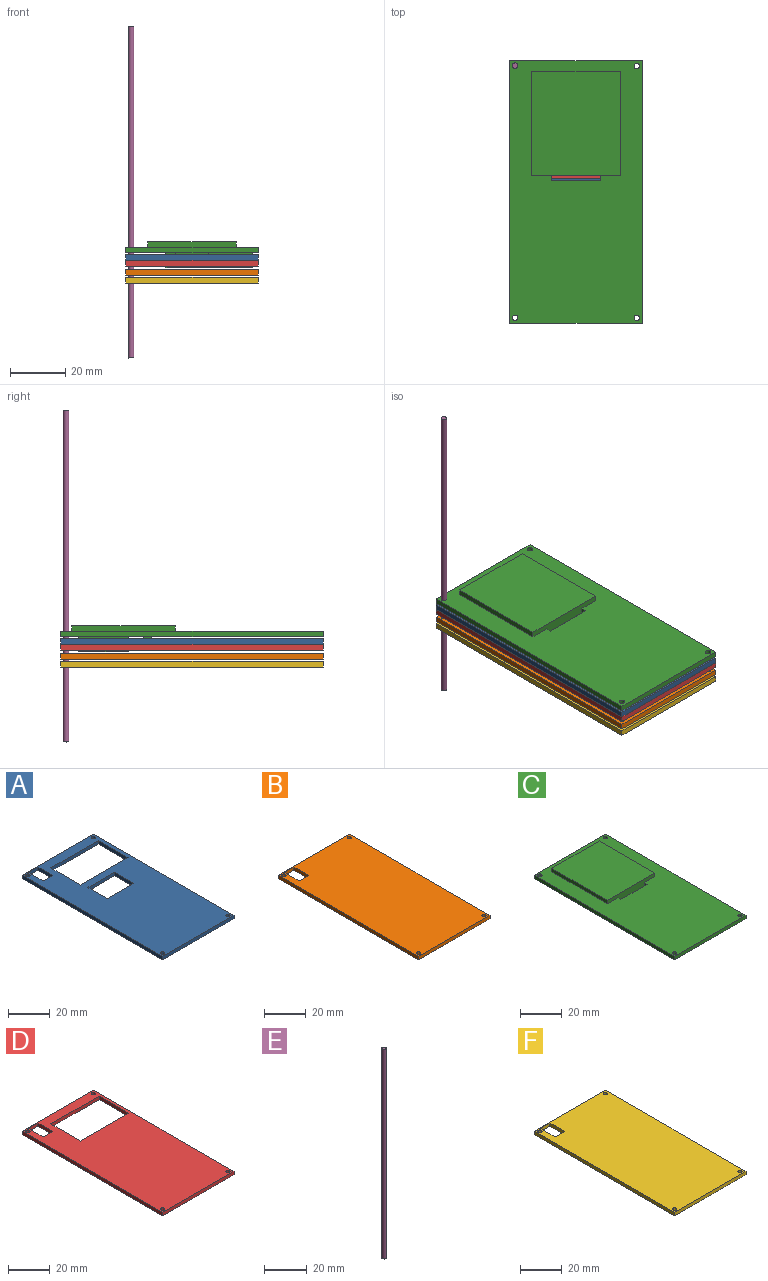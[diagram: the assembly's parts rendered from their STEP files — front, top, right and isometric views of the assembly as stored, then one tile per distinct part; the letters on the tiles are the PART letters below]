
ASSEMBLY  parts=6 mates=6
PART A: 22 faces, bbox 48x95x2 mm
  f0: plane 95x48mm, normal (0,0,1), area 3609.4mm2, adj f2,f3,f4,f5,f6,f7,f8,f9
  f1: plane 95x48mm, normal (0,0,-1), area 3609.4mm2, adj f2,f3,f4,f5,f6,f7,f8,f9
  f2: plane 48x2mm, normal (0,-1,0), area 96mm2, adj f0,f1,f3,f8
  f3: plane 95x2mm, normal (1,0,0), area 190mm2, adj f0,f1,f2,f4
  f4: plane 48x2mm, normal (0,1,0), area 96mm2, adj f0,f1,f3,f8
  f5: cylinder r=1mm len=2mm, axis (0,0,-1), area 12.6mm2, adj f0,f1
  f6: cylinder r=1mm len=2mm, axis (0,0,-1), area 12.6mm2, adj f0,f1
  f7: cylinder r=1mm len=2mm, axis (0,0,-1), area 12.6mm2, adj f0,f1
  f8: plane 95x2mm, normal (-1,0,0), area 190mm2, adj f0,f1,f2,f4
  f9: cylinder r=1mm len=2mm, axis (0,0,-1), area 12.6mm2, adj f0,f1
  f10: plane 18x2mm, normal (0,1,0), area 36mm2, adj f0,f1,f11,f13
  f11: plane 13x2mm, normal (1,0,0), area 26mm2, adj f0,f1,f10,f12
  f12: plane 18x2mm, normal (0,-1,0), area 36mm2, adj f0,f1,f11,f13
  f13: plane 13x2mm, normal (-1,0,0), area 26mm2, adj f0,f1,f10,f12
  f14: plane 20x2mm, normal (1,0,0), area 40mm2, adj f0,f1,f15,f17
  f15: plane 32x2mm, normal (0,1,0), area 64mm2, adj f0,f1,f14,f16
  f16: plane 20x2mm, normal (-1,0,0), area 40mm2, adj f0,f1,f15,f17
  f17: plane 32x2mm, normal (0,-1,0), area 64mm2, adj f0,f1,f14,f16
  f18: plane 6.4x2mm, normal (0,1,0), area 12.8mm2, adj f0,f1,f19,f21
  f19: plane 10x2mm, normal (-1,0,0), area 20mm2, adj f0,f1,f18,f20
  f20: plane 6.4x2mm, normal (0,-1,0), area 12.8mm2, adj f0,f1,f19,f21
  f21: plane 10x2mm, normal (1,0,0), area 20mm2, adj f0,f1,f18,f20
PART B: 14 faces, bbox 48x95x2 mm
  f0: plane 95x2mm, normal (-1,0,0), area 190mm2, adj f1,f7,f8,f9
  f1: plane 48x2mm, normal (0,-1,0), area 96mm2, adj f0,f2,f8,f9
  f2: plane 95x2mm, normal (1,0,0), area 190mm2, adj f1,f7,f8,f9
  f3: cylinder r=1mm len=2mm, axis (0,0,-1), area 12.6mm2, adj f8,f9
  f4: cylinder r=1mm len=2mm, axis (0,0,-1), area 12.6mm2, adj f8,f9
  f5: cylinder r=1mm len=2mm, axis (0,0,-1), area 12.6mm2, adj f8,f9
  f6: cylinder r=1mm len=2mm, axis (0,0,-1), area 12.6mm2, adj f8,f9
  f7: plane 48x2mm, normal (0,1,0), area 96mm2, adj f0,f2,f8,f9
  f8: plane 95x48mm, normal (0,0,1), area 4483.4mm2, adj f0,f1,f2,f3,f4,f5,f6,f7
  f9: plane 95x48mm, normal (0,0,-1), area 4483.4mm2, adj f0,f1,f2,f3,f4,f5,f6,f7
  f10: plane 6.4x2mm, normal (0,1,0), area 12.8mm2, adj f8,f9,f11,f13
  f11: plane 10x2mm, normal (-1,0,0), area 20mm2, adj f8,f9,f10,f12
  f12: plane 6.4x2mm, normal (0,-1,0), area 12.8mm2, adj f8,f9,f11,f13
  f13: plane 10x2mm, normal (1,0,0), area 20mm2, adj f8,f9,f10,f12
PART C: 28 faces, bbox 48x95x9.3 mm
  f0: plane 95x48mm, normal (0,0,-1), area 3910.2mm2, adj f2,f3,f4,f5,f6,f7,f8,f9
  f1: plane 95x48mm, normal (0,0,1), area 3311.4mm2, adj f2,f3,f4,f5,f6,f7,f8,f9
  f2: plane 48x2mm, normal (0,-1,0), area 96mm2, adj f0,f1,f3,f8
  f3: plane 95x2mm, normal (1,0,0), area 190mm2, adj f0,f1,f2,f4
  f4: plane 48x2mm, normal (0,1,0), area 96mm2, adj f0,f1,f3,f8
  f5: cylinder r=1mm len=2mm, axis (0,0,-1), area 12.6mm2, adj f0,f1
  f6: cylinder r=1mm len=2mm, axis (0,0,-1), area 12.6mm2, adj f0,f1
  f7: cylinder r=1mm len=2mm, axis (0,0,-1), area 12.6mm2, adj f0,f1
  f8: plane 95x2mm, normal (-1,0,0), area 190mm2, adj f0,f1,f2,f4
  f9: cylinder r=1mm len=2mm, axis (0,0,-1), area 12.6mm2, adj f0,f1
  f10: plane 18x2mm, normal (0,1,0), area 36mm2, adj f0,f1,f11,f13
  f11: plane 2x2mm, normal (1,0,0), area 4mm2, adj f0,f1,f10,f12
  f12: plane 32x4mm, normal (0,-1,0), area 100mm2, adj f0,f1,f11,f13,f14,f16,f17
  f13: plane 2x2mm, normal (-1,0,0), area 4mm2, adj f0,f1,f10,f12
  f14: plane 37.5x2mm, normal (1,0,0), area 75mm2, adj f1,f12,f15,f17
  f15: plane 32x2mm, normal (0,1,0), area 64mm2, adj f1,f14,f16,f17
  f16: plane 37.5x2mm, normal (-1,0,0), area 75mm2, adj f1,f12,f15,f17
  f17: plane 37.5x32mm, normal (0,0,1), area 1200mm2, adj f12,f14,f15,f16
  f18: plane 3x2mm, normal (-1,0,0), area 6mm2, adj f0,f19,f21,f22
  f19: plane 12x2mm, normal (0,-1,0), area 24mm2, adj f0,f18,f20,f22
  f20: plane 3x2mm, normal (1,0,0), area 6mm2, adj f0,f19,f21,f22
  f21: plane 12x2mm, normal (0,1,0), area 24mm2, adj f0,f18,f20,f22
  f22: plane 12x3mm, normal (0,0,-1), area 36mm2, adj f18,f19,f20,f21
  f23: plane 18x5.3mm, normal (-1,0,0), area 95.4mm2, adj f0,f24,f26,f27
  f24: plane 31.4x5.3mm, normal (0,-1,0), area 166.4mm2, adj f0,f23,f25,f27
  f25: plane 18x5.3mm, normal (1,0,0), area 95.4mm2, adj f0,f24,f26,f27
  f26: plane 31.4x5.3mm, normal (0,1,0), area 166.4mm2, adj f0,f23,f25,f27
  f27: plane 31.4x18mm, normal (0,0,-1), area 565.2mm2, adj f23,f24,f25,f26
PART D: 18 faces, bbox 48x95x2 mm
  f0: plane 48x2mm, normal (0,-1,0), area 96mm2, adj f1,f6,f8,f9
  f1: plane 95x2mm, normal (1,0,0), area 190mm2, adj f0,f2,f8,f9
  f2: plane 48x2mm, normal (0,1,0), area 96mm2, adj f1,f6,f8,f9
  f3: cylinder r=1mm len=2mm, axis (0,0,-1), area 12.6mm2, adj f8,f9
  f4: cylinder r=1mm len=2mm, axis (0,0,-1), area 12.6mm2, adj f8,f9
  f5: cylinder r=1mm len=2mm, axis (0,0,-1), area 12.6mm2, adj f8,f9
  f6: plane 95x2mm, normal (-1,0,0), area 190mm2, adj f0,f2,f8,f9
  f7: cylinder r=1mm len=2mm, axis (0,0,-1), area 12.6mm2, adj f8,f9
  f8: plane 95x48mm, normal (0,0,1), area 3833.4mm2, adj f0,f1,f2,f3,f4,f5,f6,f7
  f9: plane 95x48mm, normal (0,0,-1), area 3833.4mm2, adj f0,f1,f2,f3,f4,f5,f6,f7
  f10: plane 6.4x2mm, normal (0,1,0), area 12.8mm2, adj f8,f9,f11,f13
  f11: plane 10x2mm, normal (-1,0,0), area 20mm2, adj f8,f9,f10,f12
  f12: plane 6.4x2mm, normal (0,-1,0), area 12.8mm2, adj f8,f9,f11,f13
  f13: plane 10x2mm, normal (1,0,0), area 20mm2, adj f8,f9,f10,f12
  f14: plane 20x2mm, normal (1,0,0), area 40mm2, adj f8,f9,f15,f17
  f15: plane 32.5x2mm, normal (0,1,0), area 65mm2, adj f8,f9,f14,f16
  f16: plane 20x2mm, normal (-1,0,0), area 40mm2, adj f8,f9,f15,f17
  f17: plane 32.5x2mm, normal (0,-1,0), area 65mm2, adj f8,f9,f14,f16
PART E: 3 faces, bbox 2x2x120 mm
  f0: cylinder r=1mm len=120mm, axis (0,0,-1), area 754mm2, adj f1,f2
  f1: plane 2x2mm, normal (0,0,1), area 3.1mm2, adj f0
  f2: plane 2x2mm, normal (0,0,-1), area 3.1mm2, adj f0
PART F: 14 faces, bbox 48x95x2 mm
  f0: plane 95x2mm, normal (-1,0,0), area 190mm2, adj f1,f7,f8,f9
  f1: plane 48x2mm, normal (0,-1,0), area 96mm2, adj f0,f2,f8,f9
  f2: plane 95x2mm, normal (1,0,0), area 190mm2, adj f1,f7,f8,f9
  f3: cylinder r=1mm len=2mm, axis (0,0,-1), area 12.6mm2, adj f8,f9
  f4: cylinder r=1mm len=2mm, axis (0,0,-1), area 12.6mm2, adj f8,f9
  f5: cylinder r=1mm len=2mm, axis (0,0,-1), area 12.6mm2, adj f8,f9
  f6: cylinder r=1mm len=2mm, axis (0,0,-1), area 12.6mm2, adj f8,f9
  f7: plane 48x2mm, normal (0,1,0), area 96mm2, adj f0,f2,f8,f9
  f8: plane 95x48mm, normal (0,0,1), area 4483.4mm2, adj f0,f1,f2,f3,f4,f5,f6,f7
  f9: plane 95x48mm, normal (0,0,-1), area 4483.4mm2, adj f0,f1,f2,f3,f4,f5,f6,f7
  f10: plane 6.4x2mm, normal (0,1,0), area 12.8mm2, adj f8,f9,f11,f13
  f11: plane 10x2mm, normal (-1,0,0), area 20mm2, adj f8,f9,f10,f12
  f12: plane 6.4x2mm, normal (0,-1,0), area 12.8mm2, adj f8,f9,f11,f13
  f13: plane 10x2mm, normal (1,0,0), area 20mm2, adj f8,f9,f10,f12
PLACE A t=(-49.24,-191.65,86.66)mm
PLACE B t=(-149.24,-191.65,81.3)mm
PLACE C t=(0.76,-191.65,89.31)mm
PLACE D t=(-99.24,-191.65,84.56)mm
PLACE E t=(-496.24,-96.65,51.32)mm
PLACE F t=(-199.24,-191.65,78.42)mm
MATE slider D.f5 <-> E.f0  axis (0,0,1) through (-146.24,-96.65,86.56)mm
MATE slider E.f0 <-> C.f7  axis (0,0,1) through (-146.24,-96.65,171.32)mm
MATE slider E.f0 <-> F.f3  axis (0,0,-1) through (-146.24,-96.65,51.32)mm
MATE slider E.f0 <-> A.f6  axis (0,0,-1) through (-146.24,-96.65,51.32)mm
MATE slider E.f0 <-> B.f6  axis (0,0,-1) through (-146.24,-96.65,51.32)mm
MATE slider B.f6 <-> E.f0  axis (0,0,1) through (-146.24,-96.65,83.3)mm
